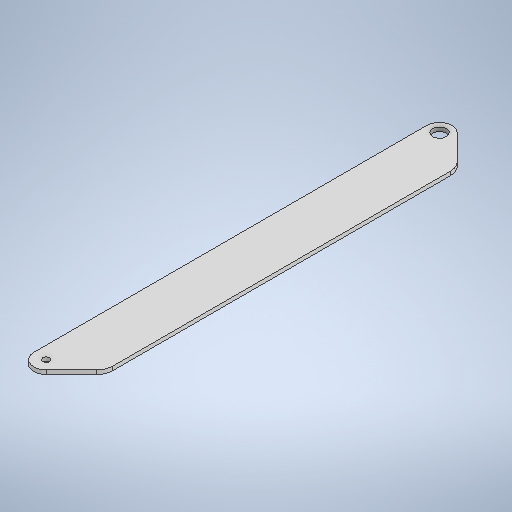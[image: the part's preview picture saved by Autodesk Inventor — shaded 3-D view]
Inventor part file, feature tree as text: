
AUTODESK INVENTOR PART (.ipt)
format: ipt  version: 2025.2 (Build 292293000, 293)  size: 265,216 bytes
history: native  units: mm
features: extrude x2, sketch x2
ambient origin geometry x8: Origin, YZ Plane, XZ Plane, XY Plane, X Axis, Y Axis, Z Axis, Center Point
bodies: Solid1 (feature_tree)
feature tree (4):
  extrude  "Extrusion1"  Depth=1.7mm TaperAngle=0.0deg
  extrude  "Extrusion2"  Depth=3.0mm
  sketch  "Sketch1"  dims[d0=10.9mm d1=170.0mm d2=0.0mm d3=12.0mm d4=12.0mm d5=5.45mm d6=45.0deg d7=7.0mm d8=7.0mm d9=10.9mm d10=135.0deg d11=1.7mm d12=0.0mm]
  sketch  "Sketch2"  dims[d13=6.0mm d14=3.0mm d15=0.0mm d16=0.0mm]
